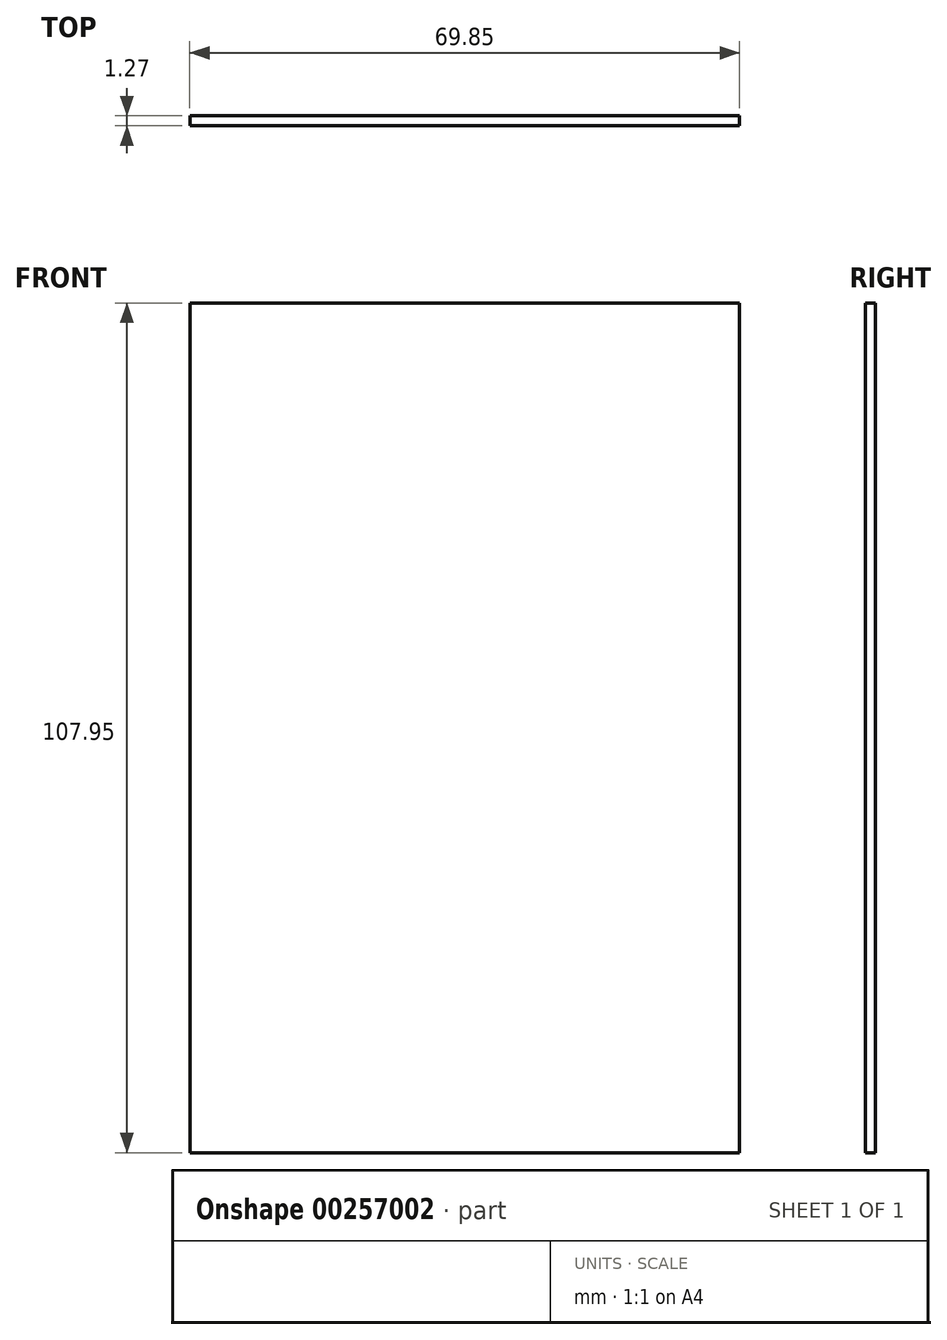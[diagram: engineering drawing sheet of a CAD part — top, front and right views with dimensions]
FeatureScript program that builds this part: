
annotation { "Feature Type Name" : "Feature", "Feature Type Description" : "" }
export const myFeature = defineFeature(function(context is Context, id is Id, definition is map)
    precondition{}
    {
        {
            var Q0;
            Q0=qCreatedBy(makeId("Front.planeOp"),FACE);
            var sketch = newSketch(context, id + "F0", { "sketchPlane" : qUnion([Q0])});
            skLineSegment(sketch, "E0.bottom", {"start": v(-61.3, -2.85) * mm, "end": v(8.55, -2.85) * mm});
            skLineSegment(sketch, "E0.top", {"start": v(-61.3, -110.8) * mm, "end": v(8.55, -110.8) * mm});
            skLineSegment(sketch, "E0.left", {"start": v(-61.3, -2.85) * mm, "end": v(-61.3, -110.8) * mm});
            skLineSegment(sketch, "E0.right", {"start": v(8.55, -2.85) * mm, "end": v(8.55, -110.8) * mm});
            skSolve(sketch);
        }
        {
            var Q0;
            Q0 = qSketchRegion(id + "F0", true);
            extrude(context, id + "F1", {"entities" : qUnion([Q0]), "depth" : 1.27 * mm});
        }
    });
